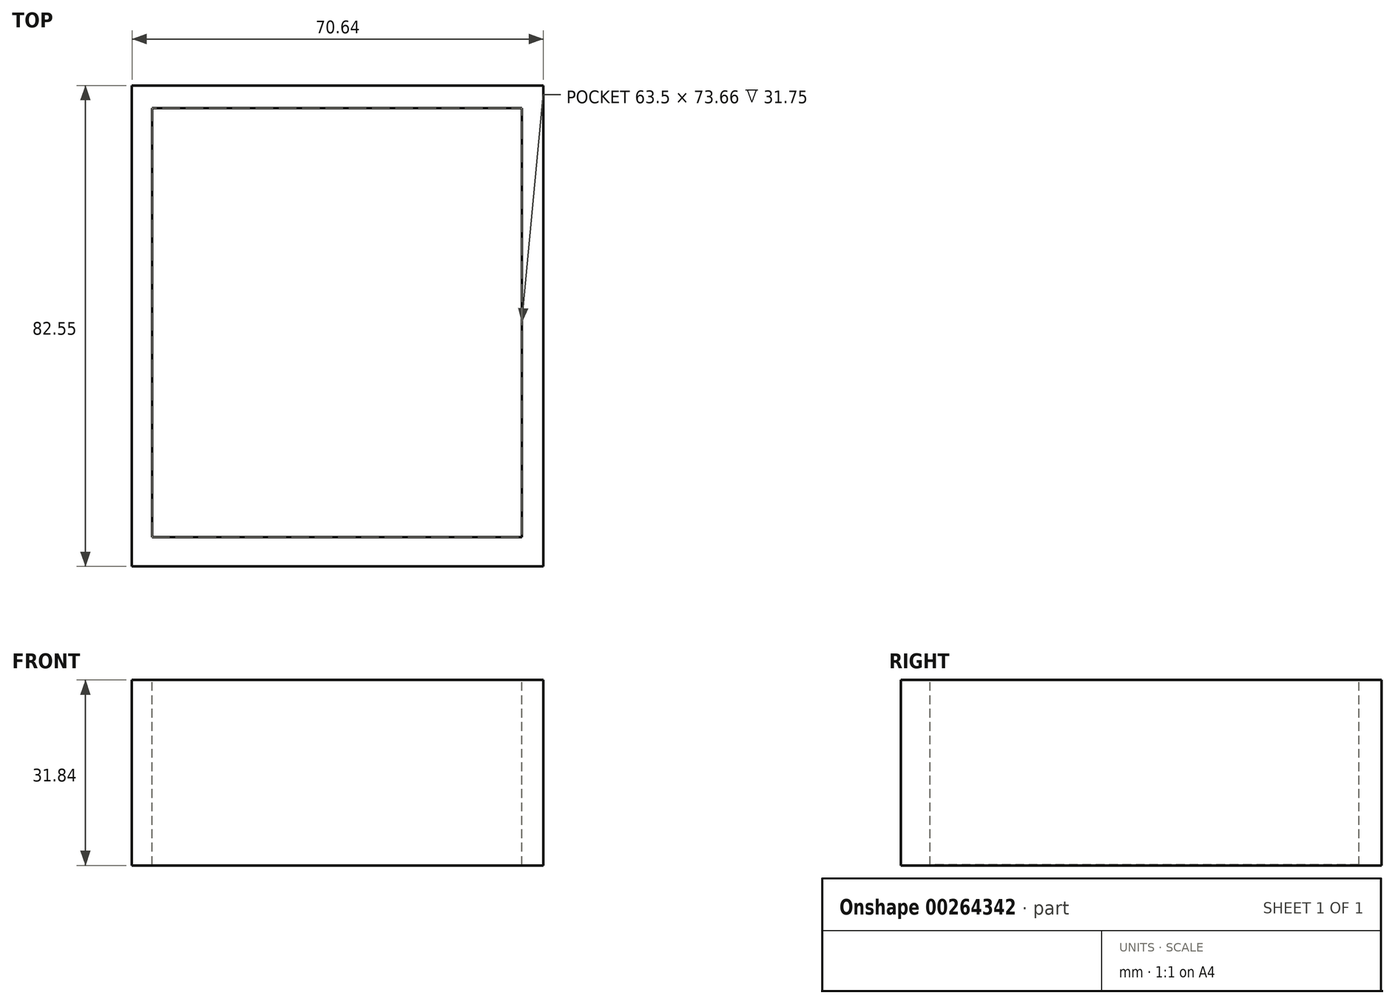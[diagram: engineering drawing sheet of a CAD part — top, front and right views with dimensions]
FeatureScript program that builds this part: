
annotation { "Feature Type Name" : "Feature", "Feature Type Description" : "" }
export const myFeature = defineFeature(function(context is Context, id is Id, definition is map)
    precondition{}
    {
        {
            var Q0;
            Q0=qCreatedBy(makeId("Front.planeOp"),FACE);
            var sketch = newSketch(context, id + "F0", { "sketchPlane" : qUnion([Q0])});
            skLineSegment(sketch, "E0.bottom", {"start": v(35.32, 15.92) * mm, "end": v(-35.32, 15.92) * mm});
            skLineSegment(sketch, "E0.top", {"start": v(35.32, -15.92) * mm, "end": v(-35.32, -15.92) * mm});
            skLineSegment(sketch, "E0.left", {"start": v(35.32, 15.92) * mm, "end": v(35.32, -15.92) * mm});
            skLineSegment(sketch, "E0.right", {"start": v(-35.32, 15.92) * mm, "end": v(-35.32, -15.92) * mm});
            skPoint(sketch, "E0.middle", {"position": v(0, 0) * mm});
            skSolve(sketch);
        }
        {
            var Q0;
            Q0 = qSketchRegion(id + "F0", true);
            extrude(context, id + "F1", {"entities" : qUnion([Q0]), "depth" : 82.55 * mm});
        }
        {
            var Q0;
            Q0=makeQuery(id+"F1.opExtrude","SWEPT_FACE",FACE,{"disambiguationData":[OSD([sQuery(id+"F0.wireOp",EDGE,"E0.bottom")])]});
            var sketch = newSketch(context, id + "F2", { "sketchPlane" : qUnion([Q0])});
            skLineSegment(sketch, "E1.bottom", {"start": v(-31.89, -3.88) * mm, "end": v(31.61, -3.88) * mm});
            skLineSegment(sketch, "E1.top", {"start": v(-31.89, -77.54) * mm, "end": v(31.61, -77.54) * mm});
            skLineSegment(sketch, "E1.left", {"start": v(-31.89, -3.88) * mm, "end": v(-31.89, -77.54) * mm});
            skLineSegment(sketch, "E1.right", {"start": v(31.61, -3.88) * mm, "end": v(31.61, -77.54) * mm});
            skSolve(sketch);
        }
        {
            var Q0;
            Q0 = qSketchRegion(id + "F2", true);
            extrude(context, id + "F3", {"entities" : qUnion([Q0]), "operationType" : NewBodyOperationType.REMOVE, "oppositeDirection" : true, "depth" : 31.75 * mm});
        }
    });
